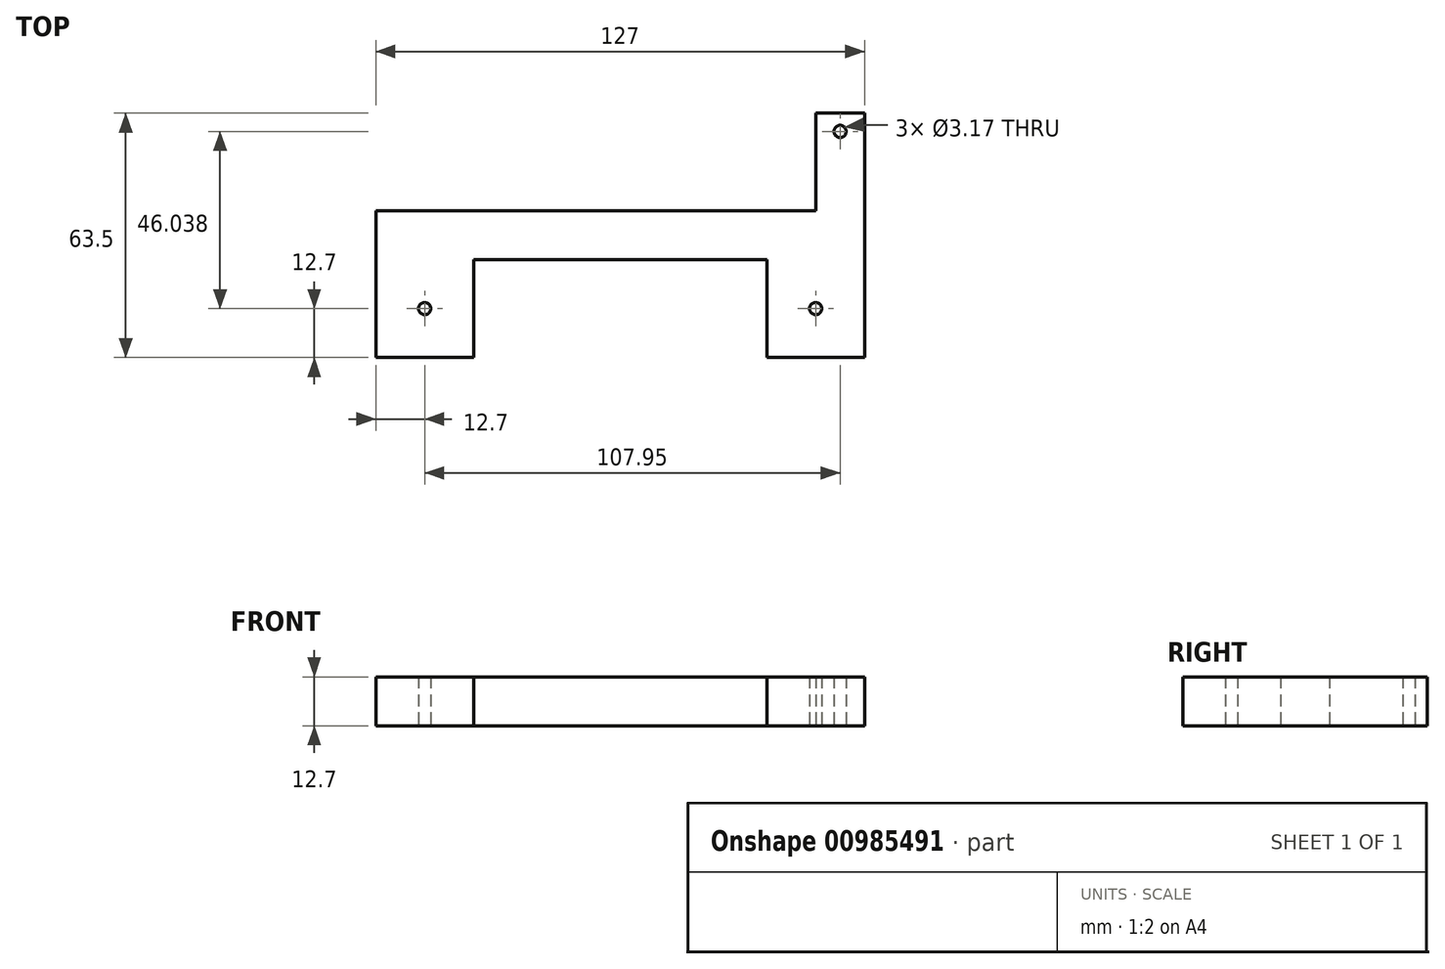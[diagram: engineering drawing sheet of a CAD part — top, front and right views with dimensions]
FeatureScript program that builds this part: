
annotation { "Feature Type Name" : "Feature", "Feature Type Description" : "" }
export const myFeature = defineFeature(function(context is Context, id is Id, definition is map)
    precondition{}
    {
        {
            var Q0;
            Q0=qCreatedBy(makeId("Top.planeOp"),FACE);
            var sketch = newSketch(context, id + "F0", { "sketchPlane" : qUnion([Q0])});
            skLineSegment(sketch, "E0.bottom", {"start": v(57.15, -6.35) * mm, "end": v(-57.15, -6.35) * mm});
            skLineSegment(sketch, "E0.top", {"start": v(57.15, 6.35) * mm, "end": v(-57.15, 6.35) * mm});
            skLineSegment(sketch, "E0.left", {"start": v(57.15, -6.35) * mm, "end": v(57.15, 6.35) * mm});
            skLineSegment(sketch, "E0.right", {"start": v(-57.15, -6.35) * mm, "end": v(-57.15, 6.35) * mm});
            skPoint(sketch, "E0.middle", {"position": v(0, 0) * mm});
            skLineSegment(sketch, "E1.bottom", {"start": v(-57.15, -6.35) * mm, "end": v(-31.75, -6.35) * mm});
            skLineSegment(sketch, "E1.top", {"start": v(-57.15, -31.75) * mm, "end": v(-31.75, -31.75) * mm});
            skLineSegment(sketch, "E1.left", {"start": v(-57.15, -6.35) * mm, "end": v(-57.15, -31.75) * mm});
            skLineSegment(sketch, "E1.right", {"start": v(-31.75, -6.35) * mm, "end": v(-31.75, -31.75) * mm});
            skLineSegment(sketch, "E2.bottom", {"start": v(57.15, -6.35) * mm, "end": v(31.75, -6.35) * mm});
            skCircle(sketch, "E3", {"center": v(-44.45, -19.05) * mm, "radius": 1.59 * mm});
            skPoint(sketch, "E3.centerSnap0", {"position": v(-57.15, -19.05) * mm});
            skPoint(sketch, "E4.centerSnap0", {"position": v(44.45, -31.75) * mm});
            skLineSegment(sketch, "E5.bottom", {"start": v(57.15, -6.35) * mm, "end": v(69.85, -6.35) * mm});
            skLineSegment(sketch, "E5.top", {"start": v(57.15, 31.75) * mm, "end": v(69.85, 31.75) * mm});
            skLineSegment(sketch, "E5.left", {"start": v(57.15, -6.35) * mm, "end": v(57.15, 31.75) * mm});
            skLineSegment(sketch, "E5.right", {"start": v(69.85, -6.35) * mm, "end": v(69.85, 31.75) * mm});
            skCircle(sketch, "E6", {"center": v(63.5, 26.99) * mm, "radius": 1.59 * mm});
            skLineSegment(sketch, "E7.bottom", {"start": v(69.85, -6.35) * mm, "end": v(44.45, -6.35) * mm});
            skLineSegment(sketch, "E7.top", {"start": v(69.85, -31.75) * mm, "end": v(44.45, -31.75) * mm});
            skLineSegment(sketch, "E7.left", {"start": v(69.85, -6.35) * mm, "end": v(69.85, -31.75) * mm});
            skLineSegment(sketch, "E7.right", {"start": v(44.45, -6.35) * mm, "end": v(44.45, -31.75) * mm});
            skCircle(sketch, "E8", {"center": v(57.15, -19.05) * mm, "radius": 1.59 * mm});
            skSolve(sketch);
        }
        {
            var Q0;
            Q0=makeQuery(id+"F0.imprint","IMPRINT",FACE,{"disambiguationData":[TD([[makeQuery(id+"F0.imprint","IMPRINT",EDGE,{"derivedFrom":sQuery(id+"F0.wireOp",EDGE,"E0.top")}),1.0]])]});
            var Q1;
            Q1=makeQuery(id+"F0.imprint","IMPRINT",FACE,{"disambiguationData":[TD([[makeQuery(id+"F0.imprint","IMPRINT",EDGE,{"derivedFrom":sQuery(id+"F0.wireOp",EDGE,"E1.top")}),1.0]])]});
            var Q2;
            {var subQ0=sQuery(id+"F0.wireOp",EDGE,"E5.bottom");Q2=makeQuery(id+"F0.imprint","IMPRINT",FACE,{"disambiguationData":[TD([[makeQuery(id+"F0.imprint","IMPRINT",EDGE,{"derivedFrom":subQ0}),-1.0]])]});}
            var Q3;
            Q3=makeQuery(id+"F0.imprint","IMPRINT",FACE,{"disambiguationData":[TD([[makeQuery(id+"F0.imprint","IMPRINT",EDGE,{"derivedFrom":sQuery(id+"F0.wireOp",EDGE,"E0.left")}),-1.0]])]});
            extrude(context, id + "F1", {"entities" : qUnion([Q0, Q1, Q2, Q3]), "depth" : 12.7 * mm, "offsetDistance" : 25.4 * mm});
        }
    });
